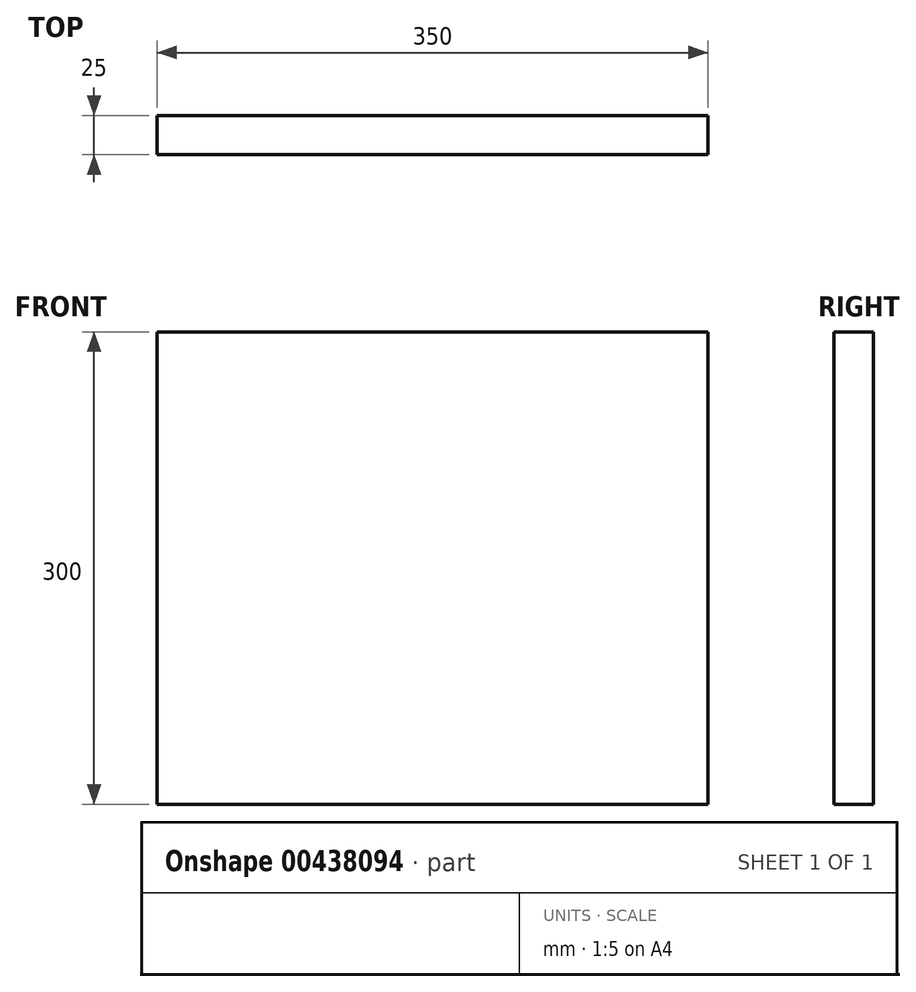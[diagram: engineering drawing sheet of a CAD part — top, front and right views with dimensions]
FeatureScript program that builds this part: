
annotation { "Feature Type Name" : "Feature", "Feature Type Description" : "" }
export const myFeature = defineFeature(function(context is Context, id is Id, definition is map)
    precondition{}
    {
        {
            var Q0;
            Q0=qCreatedBy(makeId("Front.planeOp"),FACE);
            var sketch = newSketch(context, id + "F0", { "sketchPlane" : qUnion([Q0])});
            skLineSegment(sketch, "E0.bottom", {"start": v(119.48, -142.1) * mm, "end": v(-230.52, -142.1) * mm});
            skLineSegment(sketch, "E0.top", {"start": v(119.48, 157.9) * mm, "end": v(-230.52, 157.9) * mm});
            skLineSegment(sketch, "E0.left", {"start": v(119.48, -142.1) * mm, "end": v(119.48, 157.9) * mm});
            skLineSegment(sketch, "E0.right", {"start": v(-230.52, -142.1) * mm, "end": v(-230.52, 157.9) * mm});
            skSolve(sketch);
        }
        {
            var Q0;
            Q0=makeQuery(id+"F0.imprint","IMPRINT",FACE,{"disambiguationData":[TD([[makeQuery(id+"F0.imprint","IMPRINT",EDGE,{"derivedFrom":sQuery(id+"F0.wireOp",EDGE,"E0.bottom")}),-1.0]])]});
            extrude(context, id + "F1", {"entities" : qUnion([Q0]), "depth" : 25 * mm, "offsetDistance" : 25 * mm});
        }
    });
